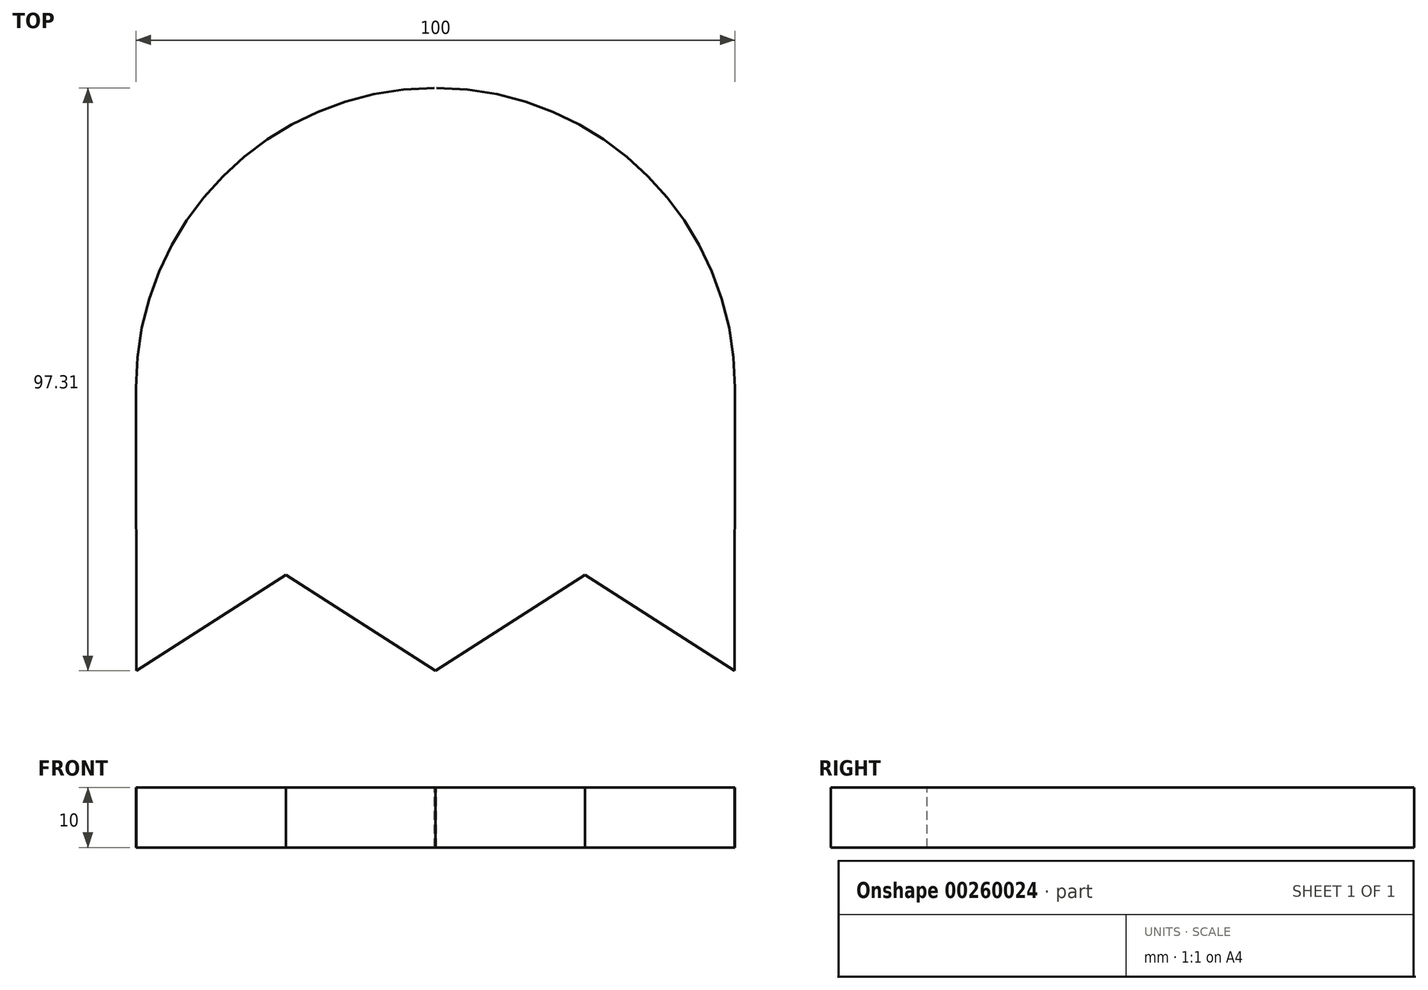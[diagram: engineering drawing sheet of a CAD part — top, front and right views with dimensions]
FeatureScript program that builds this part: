
annotation { "Feature Type Name" : "Feature", "Feature Type Description" : "" }
export const myFeature = defineFeature(function(context is Context, id is Id, definition is map)
    precondition{}
    {
        {
            var Q0;
            Q0=qCreatedBy(makeId("Top.planeOp"),FACE);
            var sketch = newSketch(context, id + "F0", { "sketchPlane" : qUnion([Q0])});
            skArc(sketch, "E0", {"start": v(-0.22, 50) * mm, "mid": v(-35.46, 35.25) * mm, "end": v(-50, -0.07) * mm});
            skLineSegment(sketch, "E1", {"start": v(-50, -0.07) * mm, "end": v(-49.94, -47.3) * mm});
            skLineSegment(sketch, "E2", {"start": v(-49.94, -47.3) * mm, "end": v(-24.96, -31.28) * mm});
            skLineSegment(sketch, "E3", {"start": v(-24.96, -31.28) * mm, "end": v(0, -47.3) * mm});
            skCircle(sketch, "E4", {"center": v(-18.7, 11.25) * mm, "radius": 11.64 * mm});
            skArc(sketch, "E5.MirrorCS", {"start": v(0.22, 50) * mm, "mid": v(35.46, 35.25) * mm, "end": v(50, -0.07) * mm});
            skLineSegment(sketch, "E6.MirrorCS", {"start": v(50, -0.07) * mm, "end": v(49.94, -47.3) * mm});
            skLineSegment(sketch, "E7.MirrorCS", {"start": v(49.94, -47.3) * mm, "end": v(24.96, -31.28) * mm});
            skLineSegment(sketch, "E8.MirrorCS", {"start": v(24.96, -31.28) * mm, "end": v(0, -47.3) * mm});
            skCircle(sketch, "E9.MirrorC", {"center": v(18.7, 11.25) * mm, "radius": 11.64 * mm});
            skSolve(sketch);
        }
        {
            var Q0;
            Q0=sQuery(id+"F0.wireOp",EDGE,"E0");
            var Q1;
            Q1=sQuery(id+"F0.wireOp",EDGE,"E5.MirrorCS");
            var Q2;
            Q2=sQuery(id+"F0.wireOp",EDGE,"E6.MirrorCS");
            var Q3;
            Q3=sQuery(id+"F0.wireOp",EDGE,"E7.MirrorCS");
            var Q4;
            Q4=sQuery(id+"F0.wireOp",EDGE,"E8.MirrorCS");
            var Q5;
            Q5=sQuery(id+"F0.wireOp",EDGE,"E3");
            var Q6;
            Q6=sQuery(id+"F0.wireOp",EDGE,"E2");
            var Q7;
            Q7=sQuery(id+"F0.wireOp",EDGE,"E1");
            extrude(context, id + "F1", {"bodyType" : ToolBodyType.SURFACE, "surfaceEntities" : qUnion([Q0, Q1, Q2, Q3, Q4, Q5, Q6, Q7]), "depth" : 10 * mm});
        }
    });
